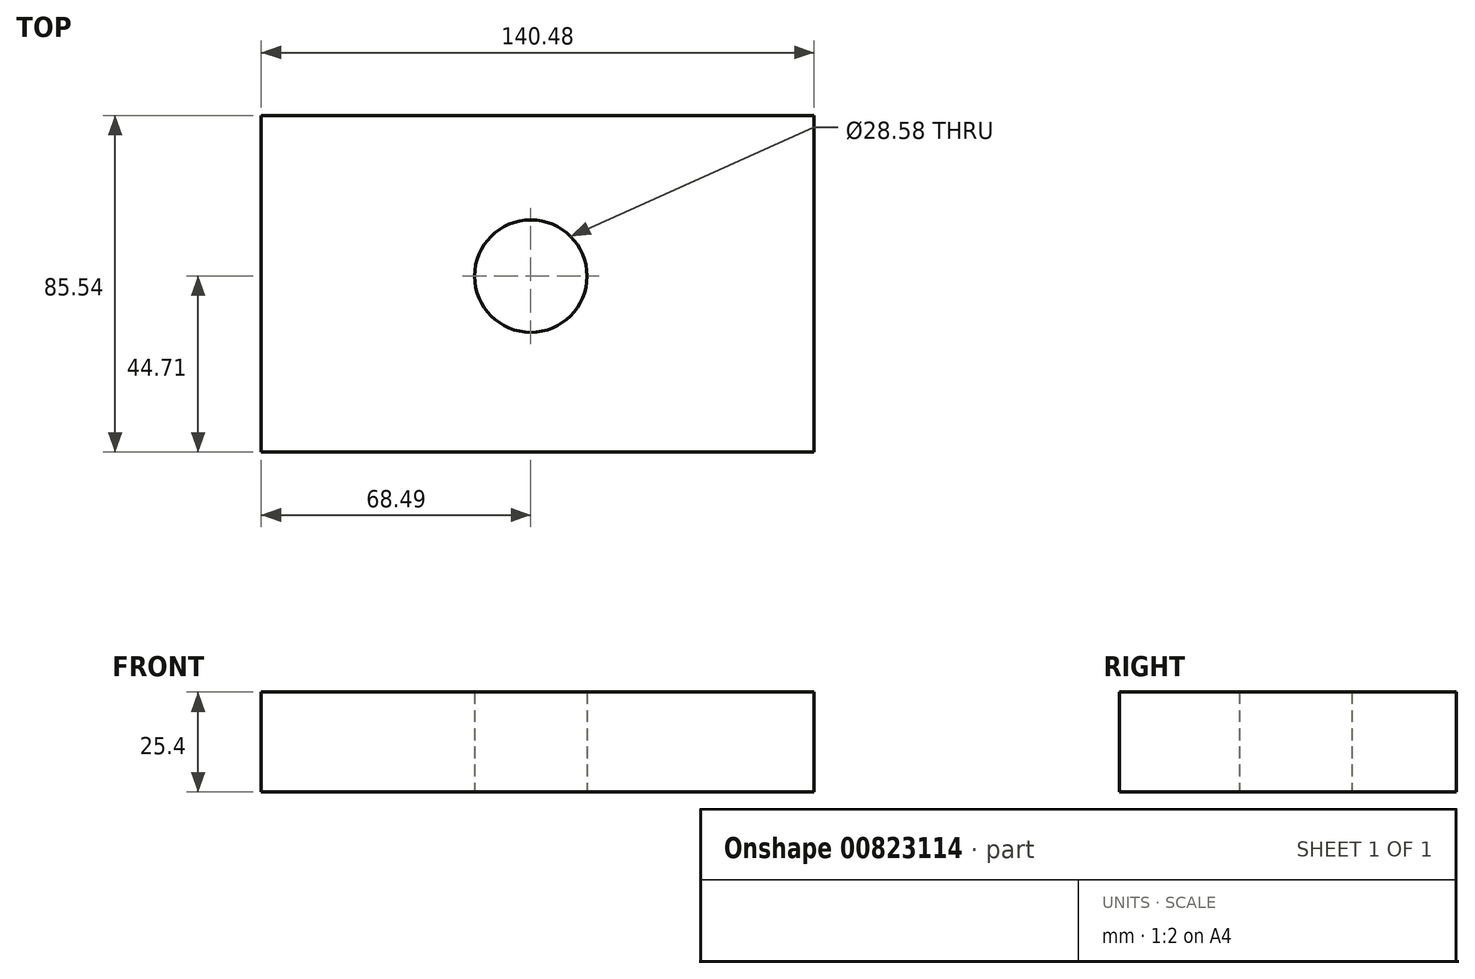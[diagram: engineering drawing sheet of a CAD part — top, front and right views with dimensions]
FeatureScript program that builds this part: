
annotation { "Feature Type Name" : "Feature", "Feature Type Description" : "" }
export const myFeature = defineFeature(function(context is Context, id is Id, definition is map)
    precondition{}
    {
        {
            var Q0;
            Q0=qCreatedBy(makeId("Top.planeOp"),FACE);
            var sketch = newSketch(context, id + "F0", { "sketchPlane" : qUnion([Q0])});
            skLineSegment(sketch, "E0.bottom", {"start": v(-68.49, 40.83) * mm, "end": v(72, 40.83) * mm});
            skLineSegment(sketch, "E0.top", {"start": v(-68.49, -44.7) * mm, "end": v(72, -44.7) * mm});
            skLineSegment(sketch, "E0.left", {"start": v(-68.49, 40.83) * mm, "end": v(-68.49, -44.7) * mm});
            skLineSegment(sketch, "E0.right", {"start": v(72, 40.83) * mm, "end": v(72, -44.7) * mm});
            skCircle(sketch, "E1", {"center": v(0, 0) * mm, "radius": 14.3 * mm});
            skSolve(sketch);
        }
        {
            var Q0;
            Q0 = qSketchRegion(id + "F0", true);
            extrude(context, id + "F1", {"entities" : qUnion([Q0]), "depth" : 25.4 * mm, "offsetDistance" : 25.4 * mm});
        }
    });
